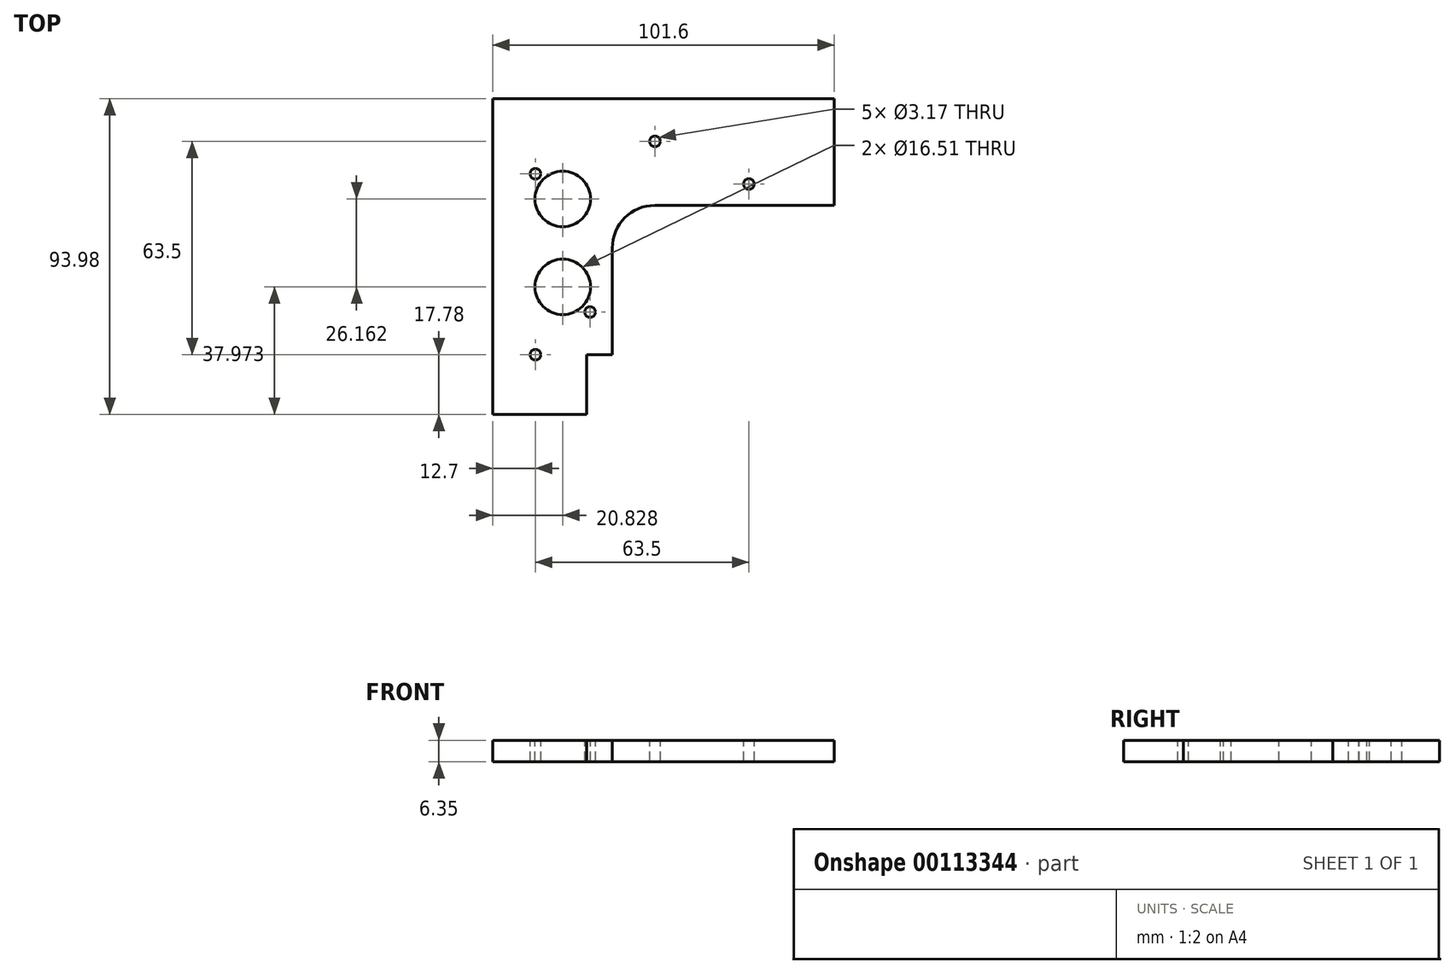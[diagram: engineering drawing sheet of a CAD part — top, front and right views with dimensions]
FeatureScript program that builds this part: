
annotation { "Feature Type Name" : "Feature", "Feature Type Description" : "" }
export const myFeature = defineFeature(function(context is Context, id is Id, definition is map)
    precondition{}
    {
        {
            var Q0;
            Q0=qCreatedBy(makeId("Top.planeOp"),FACE);
            var sketch = newSketch(context, id + "F0", { "sketchPlane" : qUnion([Q0])});
            skLineSegment(sketch, "E0.bottom", {"start": v(0, 0) * mm, "end": v(203.2, 0) * mm});
            skLineSegment(sketch, "E0.top", {"start": v(0, 93.98) * mm, "end": v(203.2, 93.98) * mm});
            skLineSegment(sketch, "E0.left", {"start": v(0, 0) * mm, "end": v(0, 93.98) * mm});
            skLineSegment(sketch, "E0.right", {"start": v(203.2, 0) * mm, "end": v(203.2, 93.98) * mm});
            skLineSegment(sketch, "E1", {"start": v(27.94, 0) * mm, "end": v(27.94, 17.78) * mm});
            skLineSegment(sketch, "E2", {"start": v(27.94, 17.78) * mm, "end": v(35.56, 17.78) * mm});
            skLineSegment(sketch, "E3", {"start": v(35.56, 17.78) * mm, "end": v(35.56, 49.53) * mm});
            skLineSegment(sketch, "E4", {"start": v(48.26, 62.23) * mm, "end": v(154.94, 62.23) * mm});
            skLineSegment(sketch, "E5", {"start": v(167.64, 49.53) * mm, "end": v(167.64, 17.78) * mm});
            skLineSegment(sketch, "E6", {"start": v(167.64, 17.78) * mm, "end": v(175.26, 17.78) * mm});
            skLineSegment(sketch, "E7", {"start": v(175.26, 17.78) * mm, "end": v(175.26, 0) * mm});
            skPoint(sketch, "E8.visualSharp", {"position": v(35.56, 62.23) * mm});
            skArc(sketch, "E8.filletArc", {"start": v(48.26, 62.23) * mm, "mid": v(39.28, 58.51) * mm, "end": v(35.56, 49.53) * mm});
            skPoint(sketch, "E9.visualSharp", {"position": v(167.64, 62.23) * mm});
            skArc(sketch, "E9.filletArc", {"start": v(167.64, 49.53) * mm, "mid": v(163.92, 58.51) * mm, "end": v(154.94, 62.23) * mm});
            skSolve(sketch);
        }
        {
            var Q0;
            Q0=makeQuery(id+"F0.imprint","IMPRINT",FACE,{"disambiguationData":[TD([[makeQuery(id+"F0.imprint","IMPRINT",EDGE,{"derivedFrom":sQuery(id+"F0.wireOp",EDGE,"E0.top")}),-1.0]])]});
            extrude(context, id + "F1", {"entities" : qUnion([Q0]), "depth" : 6.35 * mm});
        }
        {
            var Q0;
            Q0=makeQuery(id+"F1.opExtrude","CAP_FACE",FACE,{"disambiguationData":[OSD([sQuery(id+"F0.wireOp",EDGE,"E0.bottom"),sQuery(id+"F0.wireOp",EDGE,"E0.top"),sQuery(id+"F0.wireOp",EDGE,"E0.left"),sQuery(id+"F0.wireOp",EDGE,"E0.right"),sQuery(id+"F0.wireOp",EDGE,"E1"),sQuery(id+"F0.wireOp",EDGE,"E2"),sQuery(id+"F0.wireOp",EDGE,"E3"),sQuery(id+"F0.wireOp",EDGE,"E4"),sQuery(id+"F0.wireOp",EDGE,"E5"),sQuery(id+"F0.wireOp",EDGE,"E6"),sQuery(id+"F0.wireOp",EDGE,"E7"),sQuery(id+"F0.wireOp",EDGE,"E8.filletArc"),sQuery(id+"F0.wireOp",EDGE,"E9.filletArc")])],"isStart":false});
            var sketch = newSketch(context, id + "F2", { "sketchPlane" : qUnion([Q0])});
            skCircle(sketch, "E10", {"center": v(12.7, 17.78) * mm, "radius": 1.59 * mm});
            skCircle(sketch, "E11", {"center": v(28.96, 30.48) * mm, "radius": 1.59 * mm});
            skCircle(sketch, "E12", {"center": v(20.83, 37.97) * mm, "radius": 8.26 * mm});
            skCircle(sketch, "E13", {"center": v(20.83, 64.13) * mm, "radius": 8.26 * mm});
            skCircle(sketch, "E14", {"center": v(12.7, 71.63) * mm, "radius": 1.59 * mm});
            skCircle(sketch, "E15", {"center": v(48.26, 81.28) * mm, "radius": 1.59 * mm});
            skCircle(sketch, "E16", {"center": v(76.2, 68.58) * mm, "radius": 1.59 * mm});
            skCircle(sketch, "E17", {"center": v(127, 68.58) * mm, "radius": 1.59 * mm});
            skCircle(sketch, "E18", {"center": v(154.94, 81.28) * mm, "radius": 1.59 * mm});
            skCircle(sketch, "E19", {"center": v(174.24, 71.63) * mm, "radius": 1.59 * mm});
            skCircle(sketch, "E20", {"center": v(182.37, 64.14) * mm, "radius": 8.26 * mm});
            skCircle(sketch, "E21", {"center": v(182.37, 37.97) * mm, "radius": 8.26 * mm});
            skCircle(sketch, "E22", {"center": v(190.5, 30.48) * mm, "radius": 1.59 * mm});
            skCircle(sketch, "E23", {"center": v(190.5, 17.78) * mm, "radius": 1.59 * mm});
            skSolve(sketch);
        }
        {
            var Q0;
            Q0=qSketchRegion(id+"F2",true);
            extrude(context, id + "F3", {"entities" : qUnion([Q0]), "operationType" : NewBodyOperationType.REMOVE, "oppositeDirection" : true, "depth" : 6.35 * mm});
        }
        {
            var Q0;
            Q0=qCreatedBy(makeId("Top.planeOp"),FACE);
            var sketch = newSketch(context, id + "F4", { "sketchPlane" : qUnion([Q0])});
            skLineSegment(sketch, "E24.bottom", {"start": v(101.6, 0) * mm, "end": v(203.2, 0) * mm});
            skLineSegment(sketch, "E24.top", {"start": v(101.6, 93.98) * mm, "end": v(203.2, 93.98) * mm});
            skLineSegment(sketch, "E24.left", {"start": v(101.6, 0) * mm, "end": v(101.6, 93.98) * mm});
            skLineSegment(sketch, "E24.right", {"start": v(203.2, 0) * mm, "end": v(203.2, 93.98) * mm});
            skSolve(sketch);
        }
        {
            var Q0;
            Q0 = qSketchRegion(id + "F4", true);
            extrude(context, id + "F5", {"entities" : qUnion([Q0]), "operationType" : NewBodyOperationType.REMOVE, "depth" : 25.4 * mm});
        }
    });
